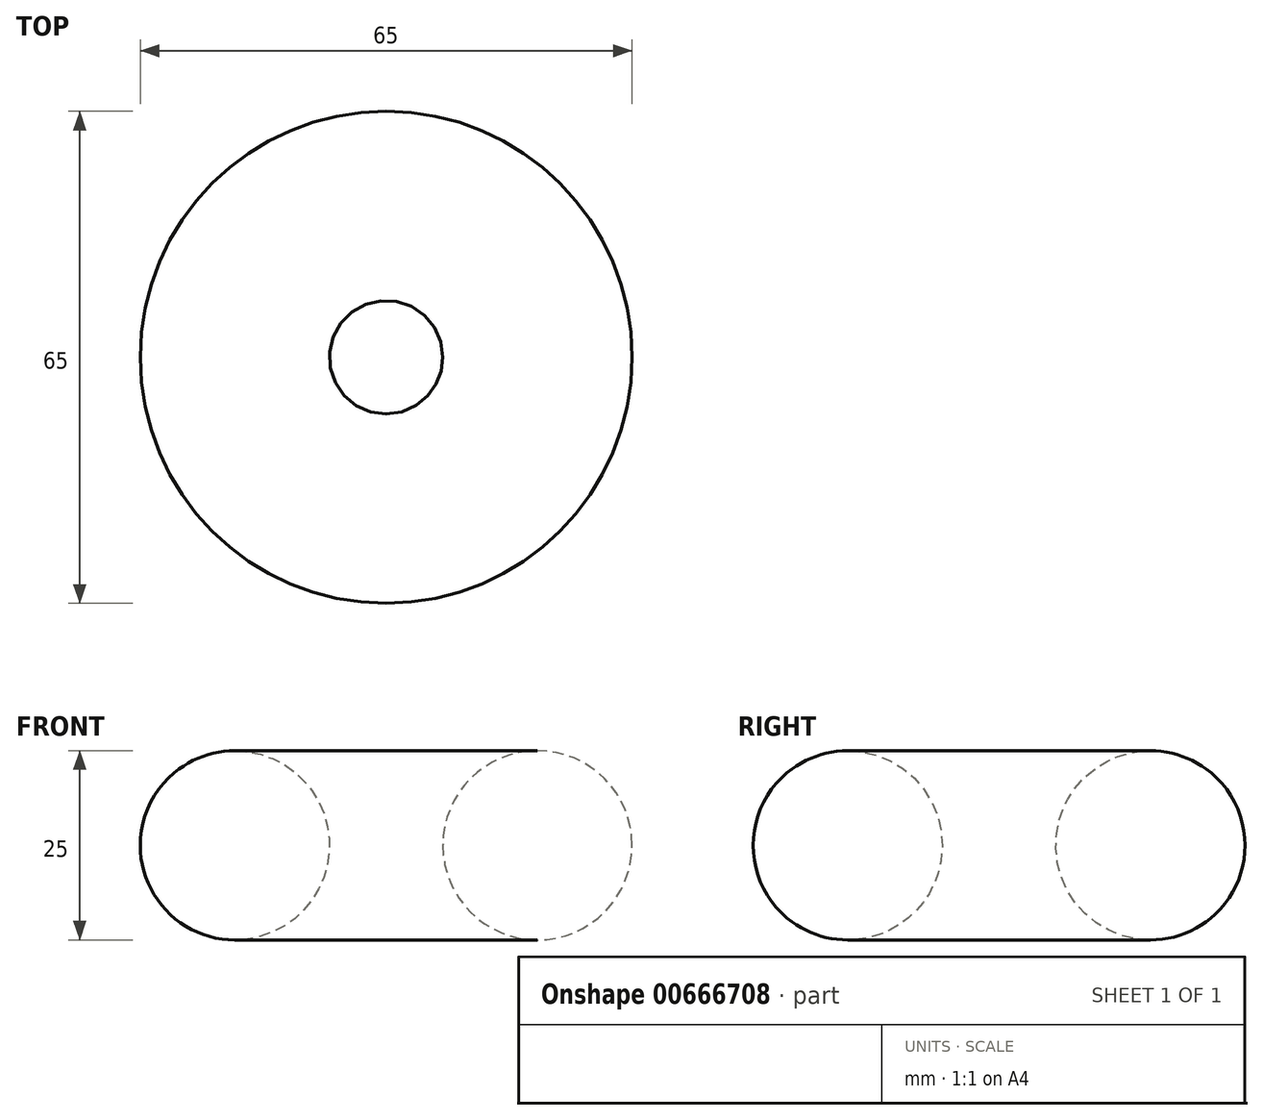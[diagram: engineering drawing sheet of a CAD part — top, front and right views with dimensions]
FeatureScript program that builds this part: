
annotation { "Feature Type Name" : "Feature", "Feature Type Description" : "" }
export const myFeature = defineFeature(function(context is Context, id is Id, definition is map)
    precondition{}
    {
        {
            var Q0;
            Q0=qCreatedBy(makeId("Right.planeOp"),FACE);
            var sketch = newSketch(context, id + "F0", { "sketchPlane" : qUnion([Q0])});
            skCircle(sketch, "E0", {"center": v(0, 0) * mm, "radius": 12.5 * mm});
            skLineSegment(sketch, "E1", {"start": v(-20, 31.42) * mm, "end": v(-20, -29.02) * mm, "construction": true});
            skSolve(sketch);
        }
        {
            var Q0;
            Q0=makeQuery(id+"F0.imprint","IMPRINT",FACE,{"disambiguationData":[TD([[makeQuery(id+"F0.imprint","IMPRINT",EDGE,{"derivedFrom":sQuery(id+"F0.wireOp",EDGE,"E0")}),1.0]])]});
            var Q1;
            Q1=sQuery(id+"F0.wireOp",EDGE,"E1");
            revolve(context, id + "F1", {"entities" : qUnion([Q0]), "axis" : qUnion([Q1]), "revolveType" : RevolveType.FULL});
        }
    });
